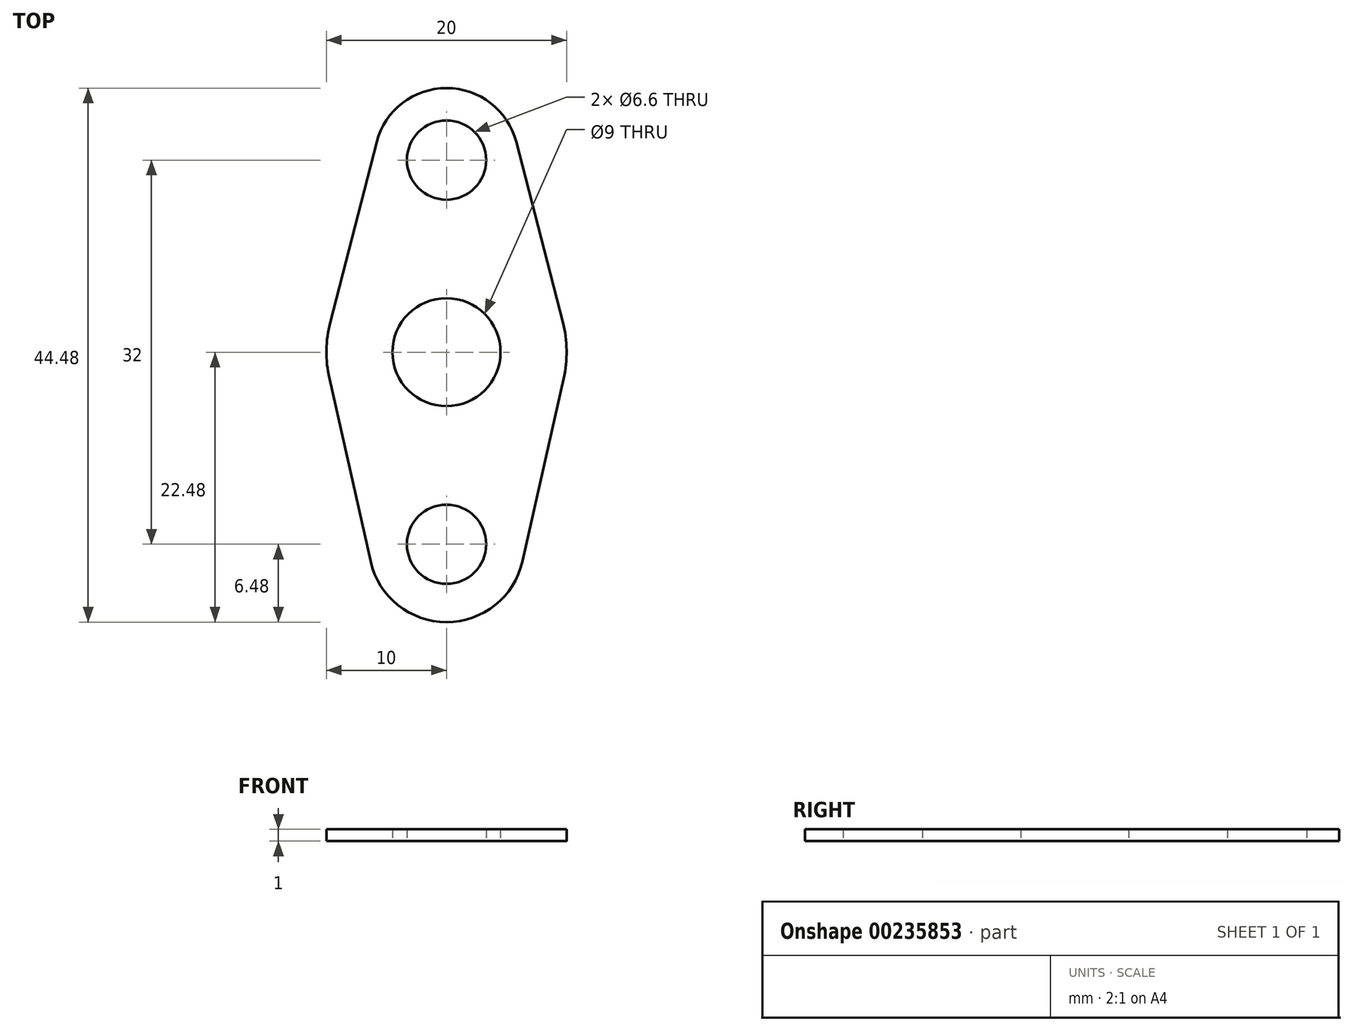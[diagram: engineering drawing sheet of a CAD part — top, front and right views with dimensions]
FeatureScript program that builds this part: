
annotation { "Feature Type Name" : "Feature", "Feature Type Description" : "" }
export const myFeature = defineFeature(function(context is Context, id is Id, definition is map)
    precondition{}
    {
        {
            var Q0;
            Q0=qCreatedBy(makeId("Top.planeOp"),FACE);
            var sketch = newSketch(context, id + "F0", { "sketchPlane" : qUnion([Q0])});
            skLineSegment(sketch, "E0", {"start": v(0, 22) * mm, "end": v(0, -22.48) * mm, "construction": true});
            skLineSegment(sketch, "E1", {"start": v(-10, 0) * mm, "end": v(10, 0) * mm, "construction": true});
            skLineSegment(sketch, "E2.0", {"start": v(-6.64, -16) * mm, "end": v(6.64, -16) * mm, "construction": true});
            skLineSegment(sketch, "E3.0", {"start": v(-6.2, 16) * mm, "end": v(6.2, 16) * mm, "construction": true});
            skCircle(sketch, "E4", {"center": v(0, 0) * mm, "radius": 4.5 * mm});
            skCircle(sketch, "E5", {"center": v(0, 16) * mm, "radius": 3.3 * mm});
            skCircle(sketch, "E6", {"center": v(0, -16) * mm, "radius": 3.3 * mm});
            skArc(sketch, "E7", {"start": v(6, 16) * mm, "mid": v(0, 22) * mm, "end": v(-6, 16) * mm});
            skArc(sketch, "E8", {"start": v(-6.48, -16) * mm, "mid": v(0, -22.48) * mm, "end": v(6.48, -16) * mm});
            skArc(sketch, "E9", {"start": v(-9.68, 2.5) * mm, "mid": v(-10, 0.15) * mm, "end": v(-9.76, -2.2) * mm});
            skLineSegment(sketch, "E10", {"start": v(-9.68, 2.5) * mm, "end": v(-5.8, 17.5) * mm});
            skLineSegment(sketch, "E11", {"start": v(5.8, 17.5) * mm, "end": v(9.68, 2.5) * mm});
            skLineSegment(sketch, "E12", {"start": v(-6.32, -17.43) * mm, "end": v(-9.76, -2.2) * mm});
            skLineSegment(sketch, "E13", {"start": v(6.32, -17.43) * mm, "end": v(9.76, -2.2) * mm});
            skArc(sketch, "E14.trimOffspring", {"start": v(9.76, -2.2) * mm, "mid": v(10, 0.15) * mm, "end": v(9.68, 2.5) * mm});
            skSolve(sketch);
        }
        {
            var Q0;
            Q0=makeQuery(id+"F0.imprint","IMPRINT",FACE,{"disambiguationData":[TD([[makeQuery(id+"F0.imprint","IMPRINT",EDGE,{"derivedFrom":sQuery(id+"F0.wireOp",EDGE,"E4")}),-1.0]])]});
            extrude(context, id + "F1", {"entities" : qUnion([Q0]), "depth" : 1 * mm, "symmetric" : true});
        }
    });
